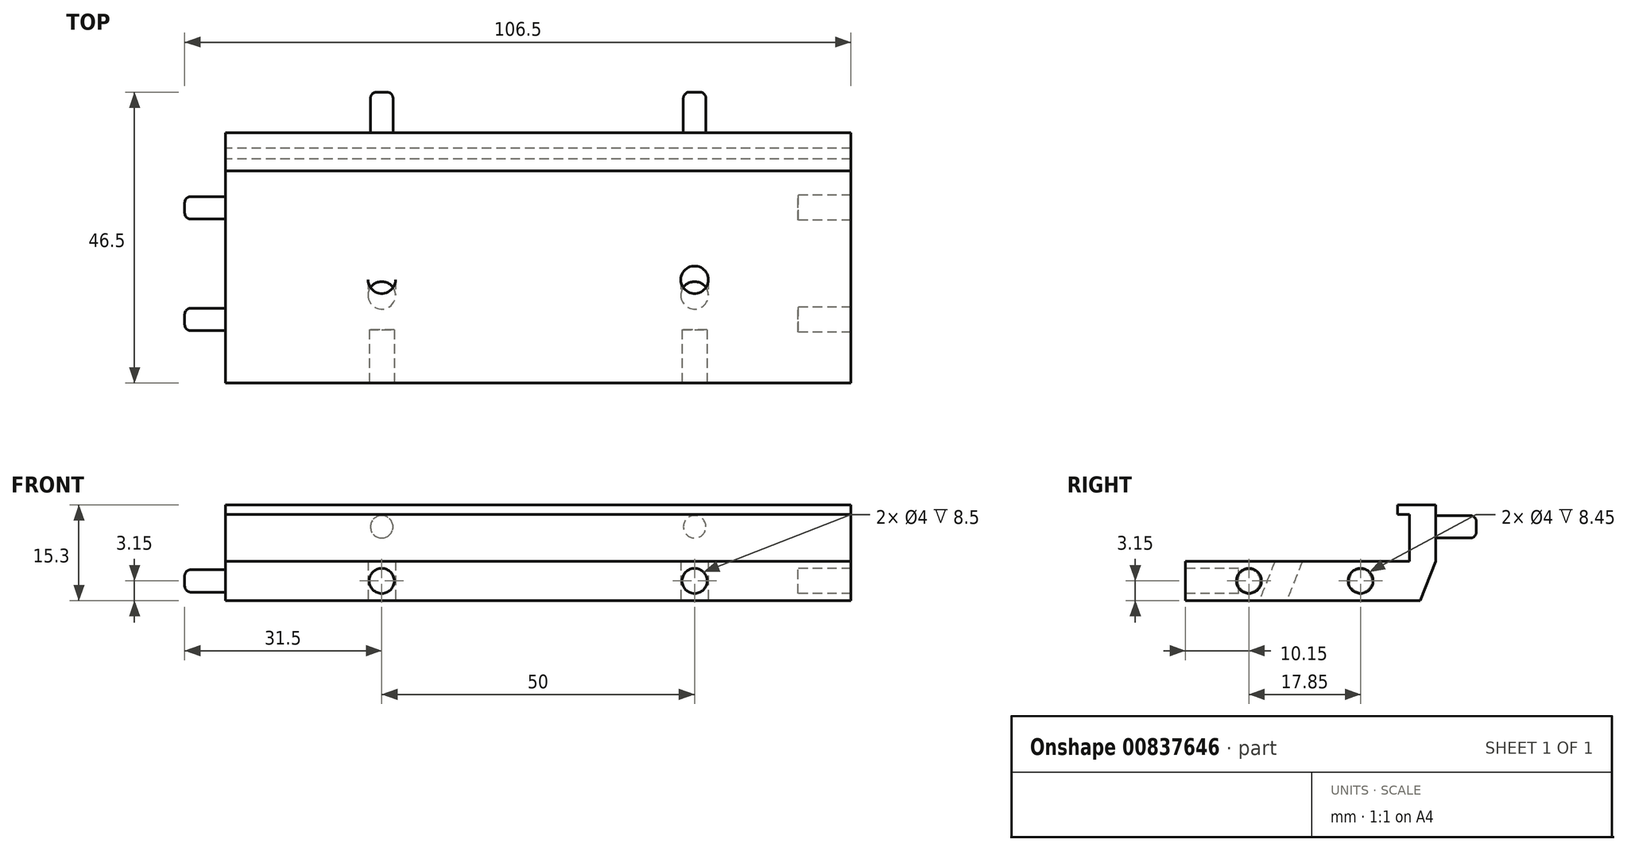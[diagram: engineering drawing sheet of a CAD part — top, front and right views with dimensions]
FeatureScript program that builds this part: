
annotation { "Feature Type Name" : "Feature", "Feature Type Description" : "" }
export const myFeature = defineFeature(function(context is Context, id is Id, definition is map)
    precondition{}
    {
        {
            var Q0;
            Q0=qCreatedBy(makeId("Right.planeOp"),FACE);
            var sketch = newSketch(context, id + "F0", { "sketchPlane" : qUnion([Q0])});
            skLineSegment(sketch, "E0", {"start": v(40, 6.3) * mm, "end": v(40, 15.3) * mm});
            skLineSegment(sketch, "E1", {"start": v(40, 15.3) * mm, "end": v(33.9, 15.3) * mm});
            skLineSegment(sketch, "E2", {"start": v(33.9, 15.3) * mm, "end": v(33.9, 13.75) * mm});
            skLineSegment(sketch, "E3", {"start": v(33.9, 13.75) * mm, "end": v(35.8, 13.75) * mm});
            skLineSegment(sketch, "E4", {"start": v(35.8, 13.75) * mm, "end": v(35.8, 6.3) * mm});
            skLineSegment(sketch, "E5", {"start": v(35.8, 6.3) * mm, "end": v(0, 6.3) * mm});
            skLineSegment(sketch, "E6", {"start": v(0, 6.3) * mm, "end": v(0, 0) * mm});
            skLineSegment(sketch, "E7", {"start": v(0, 0) * mm, "end": v(37.5, 0) * mm});
            skLineSegment(sketch, "E8", {"start": v(37.5, 0) * mm, "end": v(40, 6.3) * mm});
            skLineSegment(sketch, "E9", {"start": v(0, 3.15) * mm, "end": v(35.8, 3.15) * mm, "construction": true});
            skLineSegment(sketch, "E10", {"start": v(8.15, 6.3) * mm, "end": v(8.15, 0) * mm, "construction": true});
            skLineSegment(sketch, "E11", {"start": v(0, 5.15) * mm, "end": v(35.8, 5.15) * mm, "construction": true});
            skCircle(sketch, "E12", {"center": v(10.15, 3.15) * mm, "radius": 2 * mm});
            skPoint(sketch, "E12.first.point", {"position": v(8.15, 3.15) * mm});
            skPoint(sketch, "E12.second.point", {"position": v(12.15, 3.15) * mm});
            skPoint(sketch, "E12.third.point", {"position": v(10.15, 5.15) * mm});
            skLineSegment(sketch, "E13", {"start": v(30, 6.3) * mm, "end": v(30, 0) * mm, "construction": true});
            skCircle(sketch, "E14", {"center": v(28, 3.15) * mm, "radius": 2 * mm});
            skPoint(sketch, "E14.first.point", {"position": v(30, 3.15) * mm});
            skPoint(sketch, "E14.second.point", {"position": v(26, 3.15) * mm});
            skPoint(sketch, "E14.third.point", {"position": v(28, 5.15) * mm});
            skSolve(sketch);
        }
        {
            var Q0;
            Q0=makeQuery(id+"F0.imprint","IMPRINT",FACE,{"disambiguationData":[TD([[makeQuery(id+"F0.imprint","IMPRINT",EDGE,{"derivedFrom":sQuery(id+"F0.wireOp",EDGE,"E0")}),1.0]])]});
            extrude(context, id + "F1", {"entities" : qUnion([Q0]), "depth" : 100 * mm, "offsetDistance" : 25 * mm});
        }
        {
            var Q0;
            Q0=makeQuery(id+"F1.opExtrude","SWEPT_FACE",FACE,{"disambiguationData":[OSD([sQuery(id+"F0.wireOp",EDGE,"E5")])]});
            var sketch = newSketch(context, id + "F2", { "sketchPlane" : qUnion([Q0])});
            skLineSegment(sketch, "E15", {"start": v(0, 14.5) * mm, "end": v(100, 14.5) * mm, "construction": true});
            skLineSegment(sketch, "E16", {"start": v(77, 0) * mm, "end": v(77, 35.8) * mm, "construction": true});
            skLineSegment(sketch, "E17", {"start": v(23, 0) * mm, "end": v(23, 35.8) * mm, "construction": true});
            skLineSegment(sketch, "E18", {"start": v(27, 0) * mm, "end": v(27, 35.8) * mm, "construction": true});
            skLineSegment(sketch, "E19", {"start": v(73, 0) * mm, "end": v(73, 35.8) * mm, "construction": true});
            skCircle(sketch, "E20", {"center": v(25, 16.5) * mm, "radius": 2.2 * mm});
            skCircle(sketch, "E21", {"center": v(75, 16.5) * mm, "radius": 2.2 * mm});
            skSolve(sketch);
        }
        {
            var Q0;
            Q0=makeQuery(id+"F1.opExtrude","SWEPT_FACE",FACE,{"disambiguationData":[OSD([sQuery(id+"F0.wireOp",EDGE,"E7")])]});
            var sketch = newSketch(context, id + "F3", { "sketchPlane" : qUnion([Q0])});
            skLineSegment(sketch, "E22", {"start": v(100, -12) * mm, "end": v(0, -12) * mm, "construction": true});
            skSolve(sketch);
        }
        {
            var Q0;
            Q0=sQuery(id+"F2.wireOp",EDGE,"E15");
            var Q1;
            Q1=sQuery(id+"F3.wireOp",EDGE,"E22");
            cPlane(context, id + "F4", {"entities" : qUnion([Q0, Q1]), "cplaneType" : CPlaneType.LINE_ANGLE, "offset" : 25 * mm, "angle" : 0 * degree, "width" : 150 * mm, "height" : 150 * mm});
        }
        {
            var Q0;
            Q0=qCreatedBy(id+"F4.planeOp",FACE);
            var sketch = newSketch(context, id + "F5", { "sketchPlane" : qUnion([Q0])});
            skLineSegment(sketch, "E23", {"start": v(-100, 4.43) * mm, "end": v(0, 4.43) * mm});
            skLineSegment(sketch, "E24", {"start": v(-74.08, 11.2) * mm, "end": v(-100, 11.2) * mm});
            skLineSegment(sketch, "E25", {"start": v(-24.08, 11.2) * mm, "end": v(-74.08, 11.2) * mm});
            skLineSegment(sketch, "E26", {"start": v(0, 11.2) * mm, "end": v(-24.08, 11.2) * mm});
            skLineSegment(sketch, "E27", {"start": v(-74.08, 11.2) * mm, "end": v(-74.08, 4.43) * mm});
            skLineSegment(sketch, "E28", {"start": v(-74.08, 4.43) * mm, "end": v(-74.08, -4.21) * mm});
            skLineSegment(sketch, "E29", {"start": v(-24.08, 11.2) * mm, "end": v(-24.08, -2.31) * mm});
            skSolve(sketch);
        }
        {
            var Q0;
            Q0=makeQuery(id+"F1.opExtrude","CAP_FACE",FACE,{"disambiguationData":[OSD([sQuery(id+"F0.wireOp",EDGE,"E0"),sQuery(id+"F0.wireOp",EDGE,"E1"),sQuery(id+"F0.wireOp",EDGE,"E2"),sQuery(id+"F0.wireOp",EDGE,"E3"),sQuery(id+"F0.wireOp",EDGE,"E4"),sQuery(id+"F0.wireOp",EDGE,"E5"),sQuery(id+"F0.wireOp",EDGE,"E6"),sQuery(id+"F0.wireOp",EDGE,"E7"),sQuery(id+"F0.wireOp",EDGE,"E8"),sQuery(id+"F0.wireOp",EDGE,"E12"),sQuery(id+"F0.wireOp",EDGE,"E14")])],"isStart":true});
            var sketch = newSketch(context, id + "F6", { "sketchPlane" : qUnion([Q0])});
            skCircle(sketch, "E30.0", {"center": v(-28, 3.15) * mm, "radius": 2 * mm});
            skCircle(sketch, "E31.0", {"center": v(-10.15, 3.15) * mm, "radius": 2 * mm});
            skCircle(sketch, "E32.0", {"center": v(-28, 3.15) * mm, "radius": 1.8 * mm});
            skCircle(sketch, "E33.0", {"center": v(-10.15, 3.15) * mm, "radius": 1.8 * mm});
            skSolve(sketch);
        }
        {
            var Q0;
            Q0=makeQuery(id+"F6.imprint","IMPRINT",FACE,{"disambiguationData":[TD([[makeQuery(id+"F6.imprint","IMPRINT",EDGE,{"derivedFrom":sQuery(id+"F6.wireOp",EDGE,"E30.0")}),-1.0]])]});
            var Q1;
            Q1=makeQuery(id+"F6.imprint","IMPRINT",FACE,{"disambiguationData":[TD([[makeQuery(id+"F6.imprint","IMPRINT",EDGE,{"derivedFrom":sQuery(id+"F6.wireOp",EDGE,"E31.0")}),-1.0]])]});
            var Q2;
            Q2=makeQuery(id+"F6.imprint","IMPRINT",FACE,{"disambiguationData":[TD([[makeQuery(id+"F6.imprint","IMPRINT",EDGE,{"derivedFrom":sQuery(id+"F6.wireOp",EDGE,"E32.0")}),1.0]])]});
            var Q3;
            Q3=makeQuery(id+"F6.imprint","IMPRINT",FACE,{"disambiguationData":[TD([[makeQuery(id+"F6.imprint","IMPRINT",EDGE,{"derivedFrom":sQuery(id+"F6.wireOp",EDGE,"E33.0")}),1.0]])]});
            var Q4;
            Q4=sQuery(id+"F6.wireOp",EDGE,"E30.0");
            extrude(context, id + "F7", {"entities" : qUnion([Q0, Q1, Q2, Q3]), "operationType" : NewBodyOperationType.ADD, "surfaceEntities" : qUnion([Q4]), "oppositeDirection" : true, "depth" : 91.55 * mm, "offsetDistance" : 25 * mm});
        }
        {
            var Q0;
            Q0=makeQuery(id+"F6.imprint","IMPRINT",FACE,{"disambiguationData":[TD([[makeQuery(id+"F6.imprint","IMPRINT",EDGE,{"derivedFrom":sQuery(id+"F6.wireOp",EDGE,"E32.0")}),1.0]])]});
            var Q1;
            Q1=makeQuery(id+"F6.imprint","IMPRINT",FACE,{"disambiguationData":[TD([[makeQuery(id+"F6.imprint","IMPRINT",EDGE,{"derivedFrom":sQuery(id+"F6.wireOp",EDGE,"E33.0")}),1.0]])]});
            var Q2;
            Q2=sQuery(id+"F6.wireOp",EDGE,"E32.0");
            extrude(context, id + "F8", {"entities" : qUnion([Q0, Q1]), "operationType" : NewBodyOperationType.ADD, "surfaceEntities" : qUnion([Q2]), "depth" : 6.5 * mm, "offsetDistance" : 25 * mm});
        }
        {
            var Q0;
            Q0=makeQuery(id+"F8.opExtrude","CAP_EDGE",EDGE,{"disambiguationData":[OSD([sQuery(id+"F6.wireOp",EDGE,"E32.0")])],"isStart":false});
            fillet(context, id + "F9", {"entities" : qUnion([Q0]), "radius" : 1 * mm, "tangentPropagation" : true, "allowEdgeOverflow" : false});
        }
        {
            var Q0;
            Q0=makeQuery(id+"F8.opExtrude","CAP_EDGE",EDGE,{"disambiguationData":[OSD([sQuery(id+"F6.wireOp",EDGE,"E33.0")])],"isStart":false});
            fillet(context, id + "F10", {"entities" : qUnion([Q0]), "radius" : 1 * mm, "tangentPropagation" : true, "allowEdgeOverflow" : false});
        }
        {
            var Q0;
            Q0=makeQuery(id+"F2.imprint","IMPRINT",FACE,{"disambiguationData":[TD([[makeQuery(id+"F2.imprint","IMPRINT",EDGE,{"derivedFrom":sQuery(id+"F2.wireOp",EDGE,"E20")}),1.0]])]});
            var Q1;
            Q1=sQuery(id+"FIOvrWFH6FjeAvq_1.wireOp",EDGE,"6c61dec0-fbf0-4798-bb24-53bfbddbe8dc.0");
            var Q2;
            Q2=sQuery(id+"F5.wireOp",EDGE,"E28");
            sweep(context, id + "F11", {"operationType" : NewBodyOperationType.REMOVE, "profiles" : qUnion([Q0]), "surfaceProfiles" : qUnion([Q1]), "path" : qUnion([Q2])});
        }
        {
            var Q0;
            Q0=makeQuery(id+"F2.imprint","IMPRINT",FACE,{"disambiguationData":[TD([[makeQuery(id+"F2.imprint","IMPRINT",EDGE,{"derivedFrom":sQuery(id+"F2.wireOp",EDGE,"E21")}),1.0]])]});
            var Q1;
            Q1=sQuery(id+"F5.wireOp",EDGE,"E29");
            sweep(context, id + "F12", {"operationType" : NewBodyOperationType.REMOVE, "profiles" : qUnion([Q0]), "path" : qUnion([Q1])});
        }
        {
            var Q0;
            Q0=makeQuery(id+"F1.opExtrude","SWEPT_FACE",FACE,{"disambiguationData":[OSD([sQuery(id+"F0.wireOp",EDGE,"E6")])]});
            var sketch = newSketch(context, id + "F13", { "sketchPlane" : qUnion([Q0])});
            skLineSegment(sketch, "E34", {"start": v(23, 6.3) * mm, "end": v(23, 0) * mm, "construction": true});
            skLineSegment(sketch, "E35", {"start": v(77, 6.3) * mm, "end": v(77, 0) * mm, "construction": true});
            skLineSegment(sketch, "E36", {"start": v(27, 6.3) * mm, "end": v(27, 0) * mm, "construction": true});
            skLineSegment(sketch, "E37", {"start": v(73, 6.3) * mm, "end": v(73, 0) * mm, "construction": true});
            skLineSegment(sketch, "E38", {"start": v(0, 5.15) * mm, "end": v(100, 5.15) * mm, "construction": true});
            skCircle(sketch, "E39", {"center": v(25, 3.15) * mm, "radius": 2 * mm});
            skPoint(sketch, "E39.first.point", {"position": v(23, 3.15) * mm});
            skPoint(sketch, "E39.second.point", {"position": v(27, 3.15) * mm});
            skPoint(sketch, "E39.third.point", {"position": v(25, 5.15) * mm});
            skCircle(sketch, "E40", {"center": v(75, 3.15) * mm, "radius": 2 * mm});
            skPoint(sketch, "E40.first.point", {"position": v(73, 3.15) * mm});
            skPoint(sketch, "E40.second.point", {"position": v(77, 3.15) * mm});
            skPoint(sketch, "E40.third.point", {"position": v(75, 5.15) * mm});
            skSolve(sketch);
        }
        {
            var Q0;
            Q0=makeQuery(id+"F13.imprint","IMPRINT",FACE,{"disambiguationData":[TD([[makeQuery(id+"F13.imprint","IMPRINT",EDGE,{"derivedFrom":sQuery(id+"F13.wireOp",EDGE,"E39")}),1.0]])]});
            var Q1;
            Q1=makeQuery(id+"F13.imprint","IMPRINT",FACE,{"disambiguationData":[TD([[makeQuery(id+"F13.imprint","IMPRINT",EDGE,{"derivedFrom":sQuery(id+"F13.wireOp",EDGE,"E40")}),1.0]])]});
            var Q2;
            Q2=sQuery(id+"F13.wireOp",EDGE,"E39");
            extrude(context, id + "F14", {"entities" : qUnion([Q0, Q1]), "operationType" : NewBodyOperationType.REMOVE, "surfaceEntities" : qUnion([Q2]), "oppositeDirection" : true, "depth" : 8.5 * mm, "offsetDistance" : 25 * mm});
        }
        {
            var Q0;
            Q0=makeQuery(id+"F1.opExtrude","SWEPT_FACE",FACE,{"disambiguationData":[OSD([sQuery(id+"F0.wireOp",EDGE,"E0")])]});
            var sketch = newSketch(context, id + "F15", { "sketchPlane" : qUnion([Q0])});
            skLineSegment(sketch, "E41", {"start": v(-77, 15.3) * mm, "end": v(-77, 6.3) * mm, "construction": true});
            skLineSegment(sketch, "E42", {"start": v(-73, 15.3) * mm, "end": v(-73, 6.3) * mm, "construction": true});
            skLineSegment(sketch, "E43", {"start": v(-23, 15.3) * mm, "end": v(-23, 6.3) * mm, "construction": true});
            skLineSegment(sketch, "E44", {"start": v(-27, 15.3) * mm, "end": v(-27, 6.3) * mm, "construction": true});
            skLineSegment(sketch, "E45", {"start": v(-100, 13.8) * mm, "end": v(0, 13.8) * mm, "construction": true});
            skCircle(sketch, "E46", {"center": v(-75, 11.8) * mm, "radius": 2 * mm});
            skPoint(sketch, "E46.first.point", {"position": v(-77, 11.8) * mm});
            skPoint(sketch, "E46.second.point", {"position": v(-73, 11.8) * mm});
            skPoint(sketch, "E46.third.point", {"position": v(-75, 13.8) * mm});
            skCircle(sketch, "E47", {"center": v(-25, 11.8) * mm, "radius": 2 * mm});
            skPoint(sketch, "E47.first.point", {"position": v(-27, 11.8) * mm});
            skPoint(sketch, "E47.second.point", {"position": v(-23, 11.8) * mm});
            skPoint(sketch, "E47.third.point", {"position": v(-25, 13.8) * mm});
            skCircle(sketch, "E48.0", {"center": v(-75, 11.8) * mm, "radius": 1.8 * mm});
            skLineSegment(sketch, "E49.0", {"start": v(5, 1.3) * mm, "end": v(5, 20.3) * mm});
            skLineSegment(sketch, "E49.1", {"start": v(-105, 1.3) * mm, "end": v(5, 1.3) * mm});
            skLineSegment(sketch, "E49.2", {"start": v(-105, 20.3) * mm, "end": v(-105, 1.3) * mm});
            skLineSegment(sketch, "E49.3", {"start": v(5, 20.3) * mm, "end": v(-105, 20.3) * mm});
            skCircle(sketch, "E50.0", {"center": v(-25, 11.8) * mm, "radius": 1.8 * mm});
            skSolve(sketch);
        }
        {
            var Q0;
            Q0=makeQuery(id+"F15.imprint","IMPRINT",FACE,{"disambiguationData":[TD([[makeQuery(id+"F15.imprint","IMPRINT",EDGE,{"derivedFrom":sQuery(id+"F15.wireOp",EDGE,"E48.0")}),1.0]])]});
            var Q1;
            Q1=makeQuery(id+"F15.imprint","IMPRINT",FACE,{"disambiguationData":[TD([[makeQuery(id+"F15.imprint","IMPRINT",EDGE,{"derivedFrom":sQuery(id+"F15.wireOp",EDGE,"E50.0")}),1.0]])]});
            extrude(context, id + "F16", {"entities" : qUnion([Q0, Q1]), "operationType" : NewBodyOperationType.ADD, "depth" : 6.5 * mm, "offsetDistance" : 25 * mm});
        }
        {
            var Q0;
            Q0=makeQuery(id+"F16.opExtrude","CAP_EDGE",EDGE,{"disambiguationData":[OSD([sQuery(id+"F15.wireOp",EDGE,"E48.0")])],"isStart":false});
            fillet(context, id + "F17", {"entities" : qUnion([Q0]), "radius" : 1 * mm, "tangentPropagation" : true, "allowEdgeOverflow" : false});
        }
        {
            var Q0;
            Q0=makeQuery(id+"F16.opExtrude","CAP_EDGE",EDGE,{"disambiguationData":[OSD([sQuery(id+"F15.wireOp",EDGE,"E50.0")])],"isStart":false});
            fillet(context, id + "F18", {"entities" : qUnion([Q0]), "radius" : 1 * mm, "tangentPropagation" : true, "allowEdgeOverflow" : false});
        }
    });
